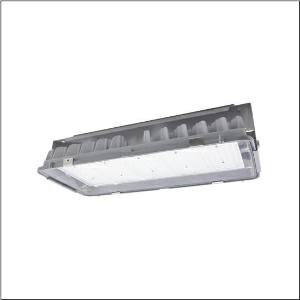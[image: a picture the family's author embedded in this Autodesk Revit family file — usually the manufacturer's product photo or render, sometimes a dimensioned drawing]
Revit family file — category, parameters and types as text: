
# Revit family: highbay_11xtreme_51hf62da4mma
name_source: partatom
category: Lighting Fixtures
units: mm (PartAtom-declared; Revit-internal decimal feet)

## family parameters
Cut with Voids When Loaded = No
Host = Face
Light Source = No
Part Type = Normal
Room Calculation Point = No
Round Connector Dimension = Use Diameter
Shared = No

## types (1)
- --- (1 x LED, 31100 lm, 170.9 W, 4000K)
    Apparent Load = 171 VA
    CIE Flux Codes = 84 96 100 100 100
    Color Rendering = 80
    Color Temperature = 4000K
    Default Elevation = 1800 mm
    Description = Highbay 11Xtreme, LED high bay luminaire, primary light control with lens, of PMMA, primary optical cover: cover, of toughened safety glass, light emission: direct distribution, primary light characteristic: symmetric, installation type: suspended mounting, surface-mounted, 1x LED module,for 1x LED, rated luminous flux: 31.100lm, luminous efficacy: 182lm/W, light colour: 840, colour temperature: 4000K, with cable H07RN-F 5x 1.5mm², mains connection: 220..240V, AC, 50/60Hz, cable length: 1,5m, rated input power: 171W, luminaire housing, of diecast aluminium, coated, silver, length: 595mm, width: 280mm, height: 195mm, protection rating (complete): IP66, insulation class (complete): insulation class I (protective earthing), certification: CE, ENEC, UKCA, protection symbol: D, ball protection: ball impact resistant according to DIN VDE 0710 part 13 (with chain suspension), impact resistance: IK08, permissible operating ambient temperature: -25..+60°C, reducing of maximum allowable ambient temperature of 5°C with ceiling mounting, packaging unit: 1 piece
    Height = 157 mm
    Lamp = 1 x LED
    Lamp Light Flux = 31100 lm
    Lamp Power = 170.9 W
    Lamp count = 1
    Length = 593 mm
    Luminous efficacy = 182 lm/W
    Manufacturer = Siteco
    ModVariant = No
    Model = 51HF62DA4MMA
    Mounting Place = Ceiling
    Mounting Type = Pendant
    Number of Poles = 1
    OnlyDefault = Yes
    Power Factor = 1
    Product Name = Highbay 11Xtreme
    Product group = LED high bay luminaire
    ProductGroupID = 903
    Protection Class = Protection class I
    Protection Degree = IP 66
    RLX_Detail_Level = 1
    RLX_Emergency_Light_Flux = 0 lm
    RLX_Emergency_Type = 0
    RLX_Emergency_Type_DB = No
    RlxData = <blob elided: 28317 chars, md5=41e72e99>
    Socket = socket
    Standby Power = 0 W
    System Light Flux = 31100 lm
    System Power = 171 W
    Type Comments = factory setting: luminous flux: 100 % | dim-lin: 254 | 1133 mA
    Type Image = l_1258342.jpg
    URL = http://relux.com
    VarID = @adj_052599
    Voltage = 0 V
    Weight = 0.00 kg
    Width = 568 mm

## geometry (parser evidence)
native form markers: Blend x4, Sweep x9
no freeform markers — native parametric forms only
